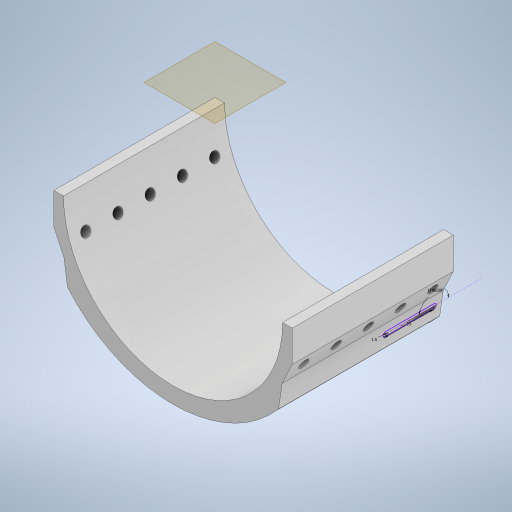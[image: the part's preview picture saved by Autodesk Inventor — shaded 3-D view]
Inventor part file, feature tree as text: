
AUTODESK INVENTOR PART (.ipt)
format: ipt  version: 2023 (Build 270158030, 158C)  size: 393,728 bytes
history: native  units: in
note: dims shown in document units (in); Inventor stores cm internally (conversion verified against a paired STEP export)
features: sketch x7, extrude x4, plane x1, sweep x1
ambient origin geometry x8: Origin, YZ Plane, XZ Plane, XY Plane, X Axis, Y Axis, Z Axis, Center Point
bodies: Solid1 (feature_tree)
feature tree (13):
  extrude  "Extrusion1"  Depth=3.5433in
  extrude  "Extrusion2"  Depth=0.1181in
  extrude  "Extrusion3"  Depth=1.9685in TaperAngle=0.0deg
  plane  "Work Plane1"
  extrude  "Extrusion5"  Depth=0.1969in
  sketch  "Sketch6"  dims[d38=0.1181in d39=0.3937in]
  sweep  "Sweep1"
  sketch  "Sketch1"  dims[d0=2.6772in d1=1.3386in d2=0.3078in d3=0.3078in d4=0.1832in d5=0.1832in d6=0.1484in d7=0.1484in d8=0.7916in d9=0.7916in d10=0.2913in d11=90.0deg d12=90.0deg d13=0.126in d14=90.0deg d15=0.126in d16=90.0deg d17=0.2707in d18=90.0deg d19=0.2707in d20=90.0deg d21=0.0787in d22=0.1969in d23=0.1969in d24=1.2297in d28=0.1575in d29=3.5433in]
  sketch  "Sketch2"  dims[d30=0.1181in d32=0.1181in]
  sketch  "Sketch3"  dims[d33=0.3836in d34=1.9685in d35=0.0in]
  sketch  "Sketch5"  dims[d36=0.1181in d37=0.1969in]
  sketch  "Sketch7"  dims[d40=0.1181in]
  sketch  "Sketch9"  dims[d41=0.3937in d42=0.1181in d43=0.3937in d44=0.1181in d45=0.3937in d46=0.0in d47=0.0in d48=0.1181in d49=0.1969in d50=0.1181in d51=0.3937in d52=0.1181in d53=0.3937in d54=0.1181in d55=0.3937in d56=0.1181in d57=0.3937in d58=0.3937in d59=0.0in d66=0.1181in d67=0.0984in d68=0.1181in d69=0.1181in d70=0.0984in d71=0.1575in d72=0.0in d73=0.5906in d74=180.0deg d75=0.0591in d77=0.5906in d78=0.0in d79=0.0591in d80=0.0984in d81=1.6535in d82=0.0in d83=0.0in d84=0.0in]
